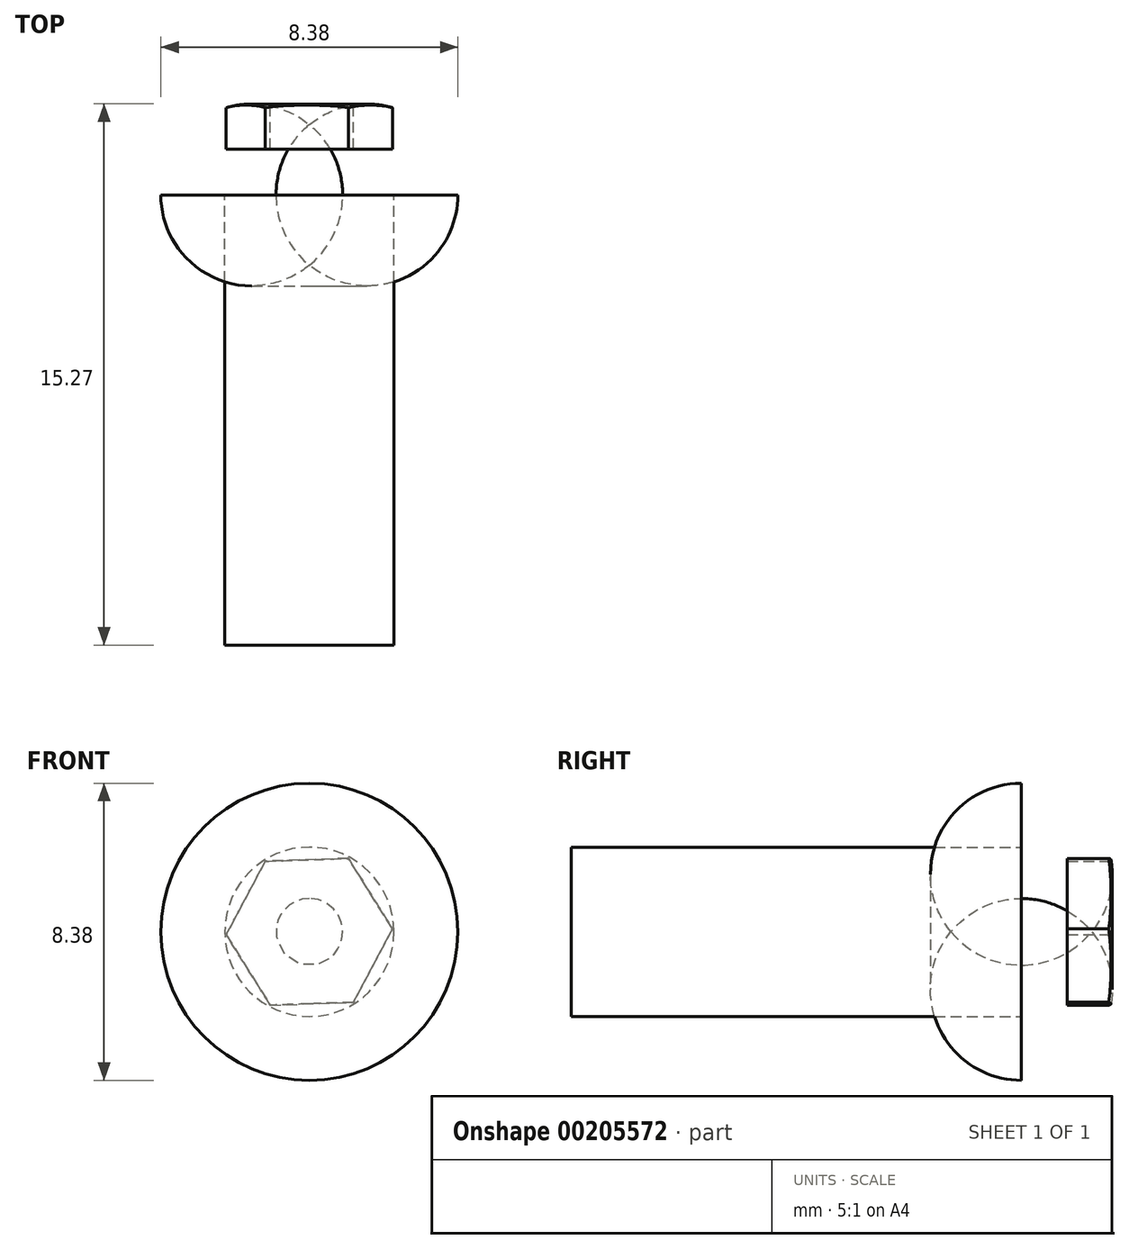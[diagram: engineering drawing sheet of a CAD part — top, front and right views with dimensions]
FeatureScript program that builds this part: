
annotation { "Feature Type Name" : "Feature", "Feature Type Description" : "" }
export const myFeature = defineFeature(function(context is Context, id is Id, definition is map)
    precondition{}
    {
        {
            var Q0;
            Q0=qCreatedBy(makeId("Front.planeOp"),FACE);
            var sketch = newSketch(context, id + "F0", { "sketchPlane" : qUnion([Q0])});
            skCircle(sketch, "E0", {"center": v(0, 0) * mm, "radius": 4.2 * mm});
            skSolve(sketch);
        }
        {
            var Q0;
            Q0=qSketchRegion(id+"F0",true);
            extrude(context, id + "F1", {"entities" : qUnion([Q0]), "oppositeDirection" : true, "depth" : 2.57 * mm});
        }
        {
            var Q0;
            Q0=makeQuery(id+"F1.opExtrude","CAP_FACE",FACE,{"disambiguationData":[OSD([sQuery(id+"F0.wireOp",EDGE,"E0")])],"isStart":true});
            var sketch = newSketch(context, id + "F2", { "sketchPlane" : qUnion([Q0])});
            skCircle(sketch, "E1", {"center": v(0, 0) * mm, "radius": 2.39 * mm});
            skSolve(sketch);
        }
        {
            var Q0;
            Q0=qSketchRegion(id+"F2",true);
            extrude(context, id + "F3", {"entities" : qUnion([Q0]), "operationType" : NewBodyOperationType.ADD, "depth" : 12.7 * mm});
        }
        {
            var Q0;
            Q0=makeQuery(id+"F1.opExtrude","CAP_FACE",FACE,{"disambiguationData":[OSD([sQuery(id+"F0.wireOp",EDGE,"E0")])],"isStart":false});
            var sketch = newSketch(context, id + "F4", { "sketchPlane" : qUnion([Q0])});
            skCircle(sketch, "E2.cCircle", {"center": v(0, 0) * mm, "radius": 2.03 * mm, "construction": true});
            skLineSegment(sketch, "E2.0", {"start": v(-1.24, -2) * mm, "end": v(-2.34, 0.08) * mm});
            skLineSegment(sketch, "E2.1", {"start": v(-2.34, 0.08) * mm, "end": v(-1.1, 2.07) * mm});
            skLineSegment(sketch, "E2.2", {"start": v(-1.1, 2.07) * mm, "end": v(1.24, 2) * mm});
            skLineSegment(sketch, "E2.3", {"start": v(1.24, 2) * mm, "end": v(2.34, -0.08) * mm});
            skLineSegment(sketch, "E2.4", {"start": v(2.34, -0.08) * mm, "end": v(1.1, -2.07) * mm});
            skLineSegment(sketch, "E2.5", {"start": v(1.1, -2.07) * mm, "end": v(-1.24, -2) * mm});
            skPoint(sketch, "E2.0.midPoint", {"position": v(-1.8, -0.95) * mm});
            skSolve(sketch);
        }
        {
            var Q0;
            Q0=qSketchRegion(id+"F4",true);
            extrude(context, id + "F5", {"entities" : qUnion([Q0]), "operationType" : NewBodyOperationType.REMOVE, "oppositeDirection" : true, "depth" : 1.27 * mm});
        }
        {
            var Q0;
            Q0=makeQuery(id+"F1.opExtrude","CAP_EDGE",EDGE,{"disambiguationData":[OSD([sQuery(id+"F0.wireOp",EDGE,"E0")])],"isStart":false});
            fillet(context, id + "F6", {"entities" : qUnion([Q0]), "radius" : 2.57 * mm, "tangentPropagation" : true, "allowEdgeOverflow" : false});
        }
    });
